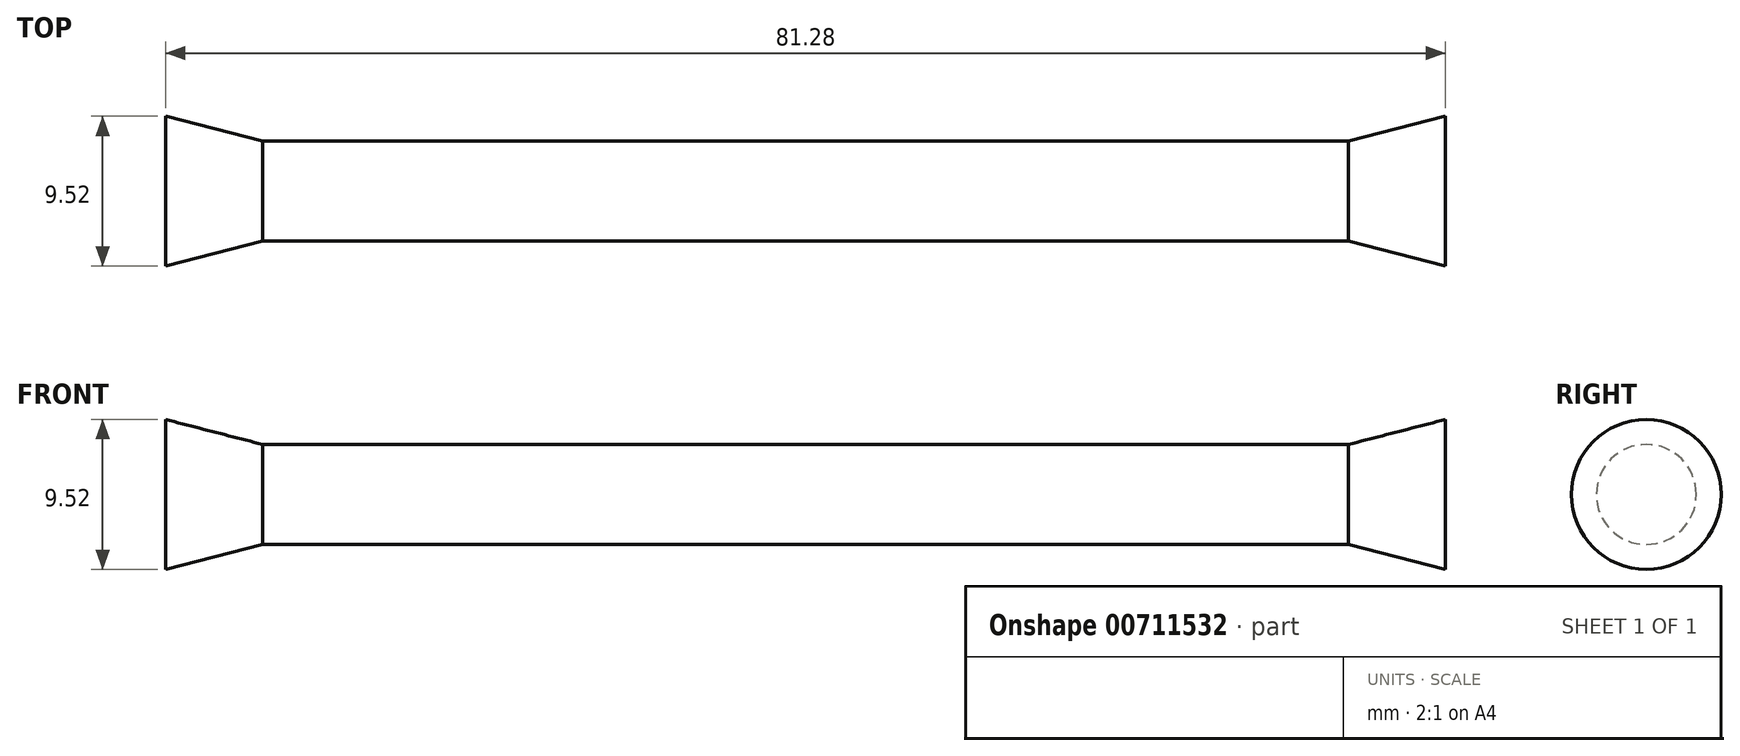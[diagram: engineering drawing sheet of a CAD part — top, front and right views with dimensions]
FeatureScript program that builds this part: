
annotation { "Feature Type Name" : "Feature", "Feature Type Description" : "" }
export const myFeature = defineFeature(function(context is Context, id is Id, definition is map)
    precondition{}
    {
        {
            var Q0;
            Q0=qCreatedBy(makeId("Top.planeOp"),FACE);
            var sketch = newSketch(context, id + "F0", { "sketchPlane" : qUnion([Q0])});
            skLineSegment(sketch, "E0", {"start": v(0, 0) * mm, "end": v(0, 4.76) * mm});
            skLineSegment(sketch, "E1", {"start": v(81.28, 4.76) * mm, "end": v(81.28, 0) * mm});
            skLineSegment(sketch, "E2", {"start": v(81.28, 0) * mm, "end": v(0, 0) * mm});
            skLineSegment(sketch, "E3.0", {"start": v(75.13, 3.17) * mm, "end": v(6.15, 3.17) * mm});
            skLineSegment(sketch, "E4", {"start": v(0, 4.76) * mm, "end": v(6.15, 3.17) * mm});
            skLineSegment(sketch, "E5", {"start": v(-12.56, 0) * mm, "end": v(92.03, 0) * mm, "construction": true});
            skLineSegment(sketch, "E6", {"start": v(81.28, 4.76) * mm, "end": v(75.13, 3.18) * mm});
            skSolve(sketch);
        }
        {
            var Q0;
            Q0 = qSketchRegion(id + "F0", true);
            var Q1;
            Q1=sQuery(id+"F0.wireOp",EDGE,"E5");
            revolve(context, id + "F1", {"surfaceOperationType" : NewSurfaceOperationType.NEW, "entities" : qUnion([Q0]), "axis" : qUnion([Q1]), "revolveType" : RevolveType.FULL});
        }
    });
